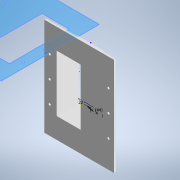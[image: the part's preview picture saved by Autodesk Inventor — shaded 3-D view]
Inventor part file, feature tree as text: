
AUTODESK INVENTOR PART (.ipt)
format: ipt  version: 2022 (Build 260153000, 153)  size: 151,040 bytes
history: native  units: mm
features: reference x10, other x5, extrude x3, sketch x3
ambient origin geometry x8: Origin, YZ Plane, XZ Plane, XY Plane, X Axis, Y Axis, Z Axis, Center Point
bodies: Body1 (feature_tree)
feature tree (21):
  other  "Твердое тело1"
  extrude  "Выдавливание1"  Depth=50.0mm
  extrude  "Выдавливание2"  Depth=110.0mm
  extrude  "Выдавливание3"  Depth=180.0mm
  sketch  "Эскиз1"
  reference  "Ссылка1"
  reference  "Ссылка2"
  reference  "Ссылка3"
  reference  "Ссылка4"
  reference  "Ссылка5"
  reference  "Ссылка6"
  reference  "Ссылка7"
  reference  "Ссылка8"
  reference  "Ссылка9"
  reference  "Ссылка10"
  sketch  "Эскиз2"
  sketch  "Эскиз3"
  other  "<path> - Robot.iam"
  other  "000.000 - Robot.iam"
  other  "000.002 - bamper:1"
  other  "rpi3-bottom:1"
note: 1 file-system path scrubbed to <path> (originals preserved in map.json)
